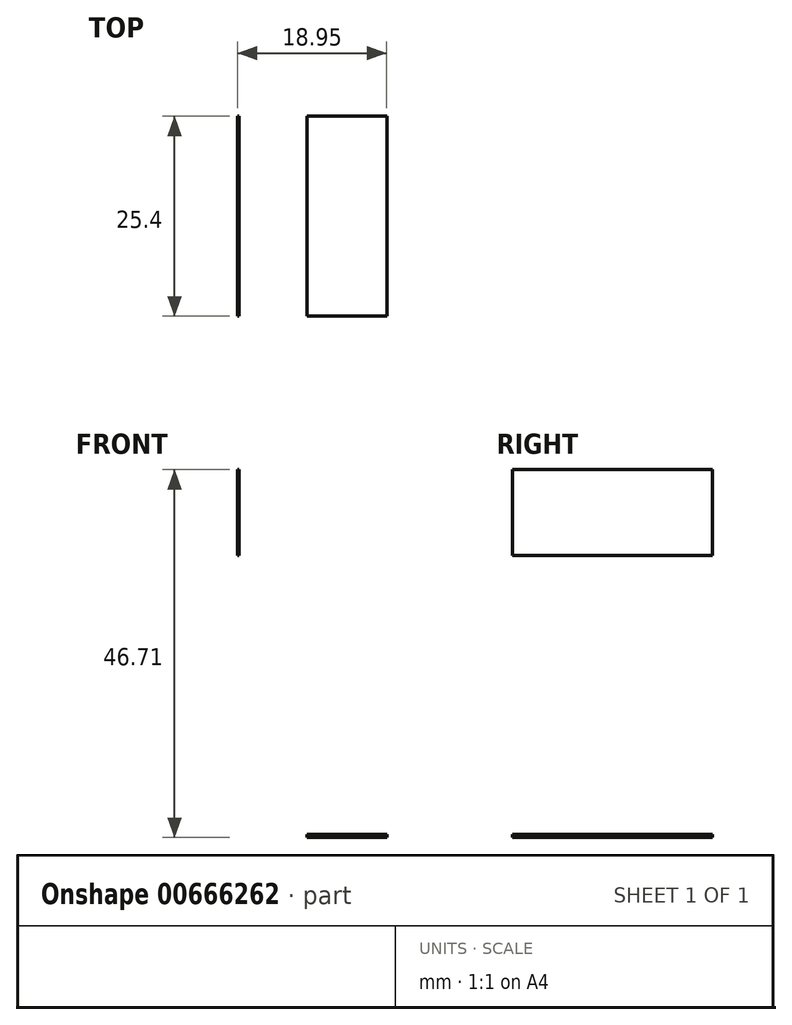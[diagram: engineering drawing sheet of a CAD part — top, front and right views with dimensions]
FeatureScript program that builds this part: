
annotation { "Feature Type Name" : "Feature", "Feature Type Description" : "" }
export const myFeature = defineFeature(function(context is Context, id is Id, definition is map)
    precondition{}
    {
        {
            var Q0;
            Q0=qCreatedBy(makeId("Front.planeOp"),FACE);
            var sketch = newSketch(context, id + "F0", { "sketchPlane" : qUnion([Q0])});
            skLineSegment(sketch, "E0.bottom", {"start": v(4.24, -53.36) * mm, "end": v(-5.92, -53.36) * mm});
            skLineSegment(sketch, "E0.top", {"start": v(4.24, -52.96) * mm, "end": v(-5.92, -52.96) * mm});
            skLineSegment(sketch, "E0.left", {"start": v(4.24, -53.36) * mm, "end": v(4.24, -52.96) * mm});
            skLineSegment(sketch, "E0.right", {"start": v(-5.92, -53.36) * mm, "end": v(-5.92, -52.96) * mm});
            skLineSegment(sketch, "E1.bottom", {"start": v(-5.92, -52.96) * mm, "end": v(-5.92, -52.96) * mm});
            skLineSegment(sketch, "E1.top", {"start": v(-5.92, -37.6) * mm, "end": v(-5.92, -37.6) * mm});
            skLineSegment(sketch, "E1.left", {"start": v(-5.92, -52.96) * mm, "end": v(-5.92, -37.6) * mm});
            skLineSegment(sketch, "E1.right", {"start": v(-5.92, -52.96) * mm, "end": v(-5.92, -37.6) * mm});
            skLineSegment(sketch, "E2.bottom", {"start": v(-5.92, -37.6) * mm, "end": v(-14.5, -37.6) * mm});
            skLineSegment(sketch, "E2.top", {"start": v(-5.92, -37.6) * mm, "end": v(-14.5, -37.6) * mm});
            skLineSegment(sketch, "E2.right", {"start": v(-14.5, -37.6) * mm, "end": v(-14.5, -37.6) * mm});
            skLineSegment(sketch, "E3.top", {"start": v(-14.5, -17.57) * mm, "end": v(-14.5, -17.57) * mm});
            skLineSegment(sketch, "E3.left", {"start": v(-14.5, -37.6) * mm, "end": v(-14.5, -17.57) * mm});
            skLineSegment(sketch, "E3.right", {"start": v(-14.5, -37.6) * mm, "end": v(-14.5, -17.57) * mm});
            skLineSegment(sketch, "E4.bottom", {"start": v(-14.7, -6.65) * mm, "end": v(-28.03, -6.65) * mm});
            skLineSegment(sketch, "E4.top", {"start": v(-14.7, -6.65) * mm, "end": v(-28.03, -6.65) * mm});
            skLineSegment(sketch, "E4.left", {"start": v(-14.7, -6.65) * mm, "end": v(-14.7, -6.65) * mm});
            skLineSegment(sketch, "E4.right", {"start": v(-28.03, -6.65) * mm, "end": v(-28.03, -6.65) * mm});
            skLineSegment(sketch, "E5.top", {"start": v(-28.03, 4.27) * mm, "end": v(-28.03, 4.27) * mm});
            skLineSegment(sketch, "E5.left", {"start": v(-28.03, -6.65) * mm, "end": v(-28.03, 4.27) * mm});
            skLineSegment(sketch, "E5.right", {"start": v(-28.03, -6.65) * mm, "end": v(-28.03, 4.27) * mm});
            skLineSegment(sketch, "E6.bottom", {"start": v(-28.03, 4.27) * mm, "end": v(-42.84, 4.27) * mm});
            skLineSegment(sketch, "E6.top", {"start": v(-28.03, 4.27) * mm, "end": v(-42.84, 4.27) * mm});
            skLineSegment(sketch, "E6.right", {"start": v(-42.84, 4.27) * mm, "end": v(-42.84, 4.27) * mm});
            skLineSegment(sketch, "E7.top", {"start": v(-42.84, 35.37) * mm, "end": v(-42.84, 35.37) * mm});
            skLineSegment(sketch, "E7.left", {"start": v(-42.84, 4.27) * mm, "end": v(-42.84, 35.37) * mm});
            skLineSegment(sketch, "E7.right", {"start": v(-42.84, 4.27) * mm, "end": v(-42.84, 35.37) * mm});
            skLineSegment(sketch, "E8.bottom", {"start": v(-14.5, -17.57) * mm, "end": v(-14.7, -17.57) * mm});
            skLineSegment(sketch, "E8.top", {"start": v(-14.5, -6.65) * mm, "end": v(-14.7, -6.65) * mm});
            skLineSegment(sketch, "E8.left", {"start": v(-14.5, -17.57) * mm, "end": v(-14.5, -6.65) * mm});
            skLineSegment(sketch, "E8.right", {"start": v(-14.7, -17.57) * mm, "end": v(-14.7, -6.65) * mm});
            skLineSegment(sketch, "E9", {"start": v(-42.84, 35.37) * mm, "end": v(-42.84, 49.43) * mm});
            skLineSegment(sketch, "E10", {"start": v(-42.84, 49.43) * mm, "end": v(-33.53, 49.43) * mm});
            skLineSegment(sketch, "E11", {"start": v(-33.53, 49.43) * mm, "end": v(-2.87, 47.04) * mm});
            skLineSegment(sketch, "E12", {"start": v(-2.87, 47.04) * mm, "end": v(-2.87, 15.93) * mm});
            skLineSegment(sketch, "E13", {"start": v(-2.87, 15.93) * mm, "end": v(12.36, 15.93) * mm});
            skLineSegment(sketch, "E14", {"start": v(12.36, 14.73) * mm, "end": v(12.36, 49.43) * mm});
            skLineSegment(sketch, "E15", {"start": v(12.36, 49.43) * mm, "end": v(50.85, 49.43) * mm});
            skLineSegment(sketch, "E16", {"start": v(50.85, 49.43) * mm, "end": v(50.85, 7.56) * mm});
            skLineSegment(sketch, "E17", {"start": v(50.85, 7.56) * mm, "end": v(39.64, 7.56) * mm});
            skLineSegment(sketch, "E18", {"start": v(39.64, 5.76) * mm, "end": v(39.64, -4.1) * mm});
            skLineSegment(sketch, "E19", {"start": v(39.64, -4.1) * mm, "end": v(23.15, -4.1) * mm});
            skLineSegment(sketch, "E20", {"start": v(23.15, -4.1) * mm, "end": v(23.15, -12.78) * mm});
            skLineSegment(sketch, "E21", {"start": v(23.15, -12.78) * mm, "end": v(13.84, -12.78) * mm});
            skLineSegment(sketch, "E22", {"start": v(13.84, -12.78) * mm, "end": v(13.84, -30.73) * mm});
            skLineSegment(sketch, "E23", {"start": v(13.63, -30.73) * mm, "end": v(6.23, -30.73) * mm});
            skLineSegment(sketch, "E24", {"start": v(6.23, -31.32) * mm, "end": v(6.23, -52.86) * mm});
            skLineSegment(sketch, "E25", {"start": v(6.23, -52.86) * mm, "end": v(4.24, -52.96) * mm});
            skSolve(sketch);
        }
        {
            var Q0;
            Q0 = qSketchRegion(id + "F0", true);
            extrude(context, id + "F1", {"entities" : qUnion([Q0]), "depth" : 25.4 * mm, "offsetDistance" : 25.4 * mm});
        }
    });
